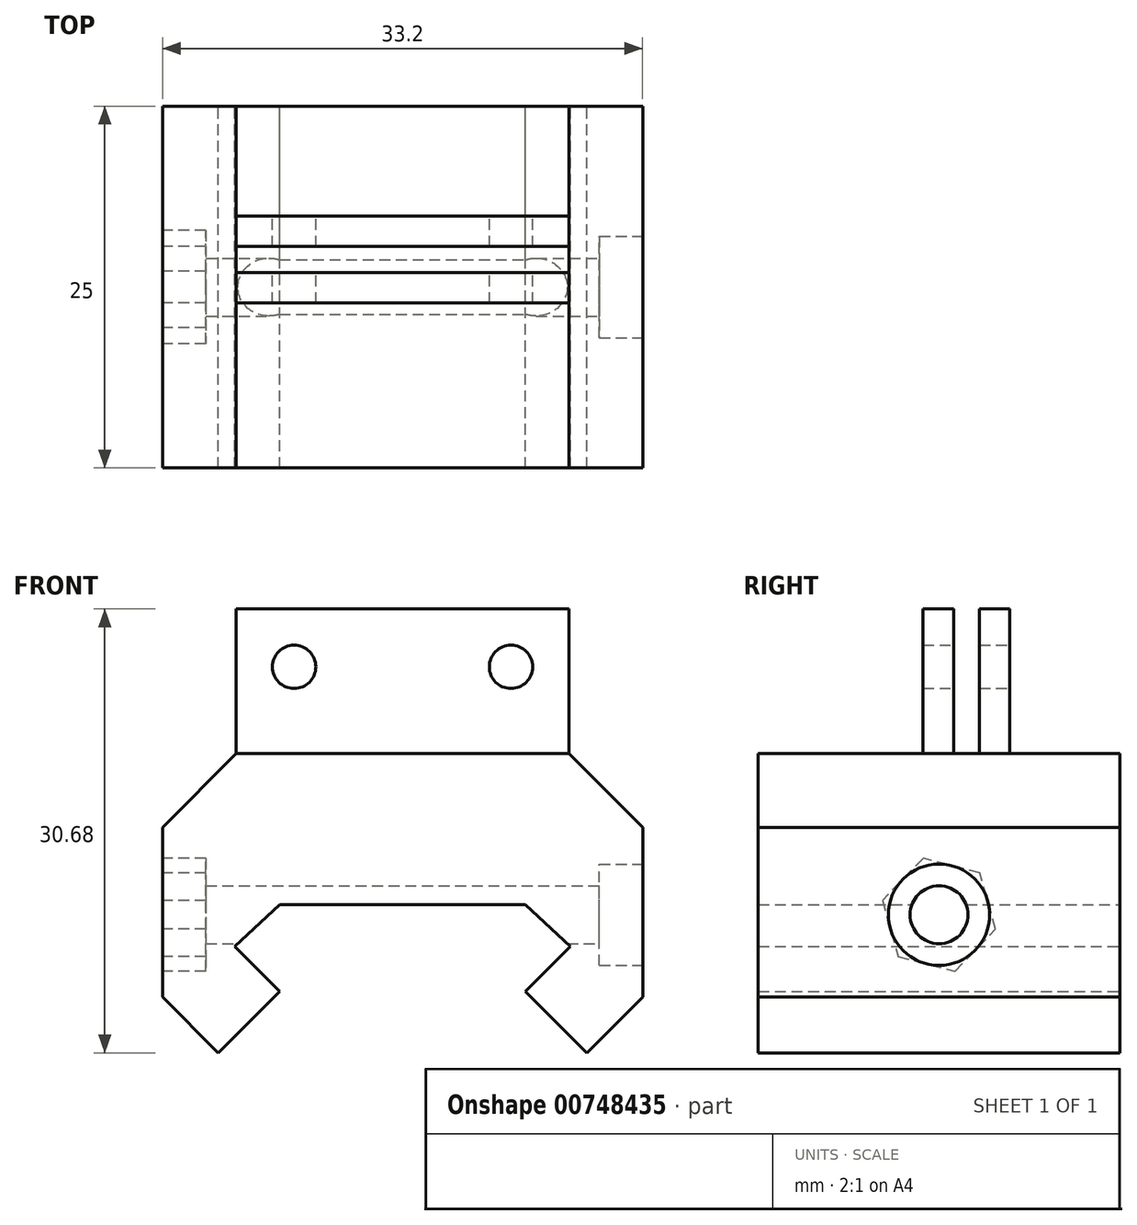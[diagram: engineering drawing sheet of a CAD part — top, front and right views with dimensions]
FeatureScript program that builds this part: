
annotation { "Feature Type Name" : "Feature", "Feature Type Description" : "" }
export const myFeature = defineFeature(function(context is Context, id is Id, definition is map)
    precondition{}
    {
        {
            var Q0;
            Q0=qCreatedBy(makeId("Front.planeOp"),FACE);
            var sketch = newSketch(context, id + "F0", { "sketchPlane" : qUnion([Q0])});
            skLineSegment(sketch, "E0", {"start": v(-8.5, 0) * mm, "end": v(8.5, 0) * mm});
            skLineSegment(sketch, "E1", {"start": v(-8.5, 0) * mm, "end": v(-11.6, -2.9) * mm});
            skLineSegment(sketch, "E2", {"start": v(-11.6, -2.9) * mm, "end": v(-8.5, -6) * mm});
            skLineSegment(sketch, "E3", {"start": v(-8.5, -6) * mm, "end": v(-12.74, -10.24) * mm});
            skLineSegment(sketch, "E4", {"start": v(-12.74, -10.24) * mm, "end": v(-22.46, -0.52) * mm});
            skLineSegment(sketch, "E5", {"start": v(-22.46, -0.52) * mm, "end": v(-11.5, 10.44) * mm});
            skLineSegment(sketch, "E6", {"start": v(-11.5, 10.44) * mm, "end": v(11.5, 10.44) * mm});
            skLineSegment(sketch, "E7", {"start": v(11.5, 10.44) * mm, "end": v(22.46, -0.52) * mm});
            skLineSegment(sketch, "E8", {"start": v(22.46, -0.52) * mm, "end": v(12.74, -10.24) * mm});
            skLineSegment(sketch, "E9", {"start": v(12.74, -10.24) * mm, "end": v(8.5, -6) * mm});
            skLineSegment(sketch, "E10", {"start": v(8.5, -6) * mm, "end": v(11.6, -2.9) * mm});
            skLineSegment(sketch, "E11", {"start": v(11.6, -2.9) * mm, "end": v(8.5, 0) * mm});
            skSolve(sketch);
        }
        {
            var Q0;
            Q0 = qSketchRegion(id + "F0", true);
            extrude(context, id + "F1", {"entities" : qUnion([Q0]), "depth" : 25 * mm, "offsetDistance" : 25 * mm});
        }
        {
            var Q0;
            Q0=makeQuery(id+"F1.opExtrude","CAP_FACE",FACE,{"disambiguationData":[OSD([sQuery(id+"F0.wireOp",EDGE,"E0"),sQuery(id+"F0.wireOp",EDGE,"E1"),sQuery(id+"F0.wireOp",EDGE,"E2"),sQuery(id+"F0.wireOp",EDGE,"E3"),sQuery(id+"F0.wireOp",EDGE,"E4"),sQuery(id+"F0.wireOp",EDGE,"E5"),sQuery(id+"F0.wireOp",EDGE,"E6"),sQuery(id+"F0.wireOp",EDGE,"E7"),sQuery(id+"F0.wireOp",EDGE,"E8"),sQuery(id+"F0.wireOp",EDGE,"E9"),sQuery(id+"F0.wireOp",EDGE,"E10"),sQuery(id+"F0.wireOp",EDGE,"E11")])],"isStart":false});
            var sketch = newSketch(context, id + "F2", { "sketchPlane" : qUnion([Q0])});
            skLineSegment(sketch, "E12.bottom", {"start": v(-24.2, 10) * mm, "end": v(-16.6, 10) * mm});
            skLineSegment(sketch, "E12.top", {"start": v(-24.2, -11.1) * mm, "end": v(-16.6, -11.1) * mm});
            skLineSegment(sketch, "E12.left", {"start": v(-24.2, 10) * mm, "end": v(-24.2, -11.1) * mm});
            skLineSegment(sketch, "E12.right", {"start": v(-16.6, 10) * mm, "end": v(-16.6, -11.1) * mm});
            skLineSegment(sketch, "E13.bottom", {"start": v(26.87, 13.5) * mm, "end": v(16.6, 13.5) * mm});
            skLineSegment(sketch, "E13.top", {"start": v(26.87, -16.6) * mm, "end": v(16.6, -16.6) * mm});
            skLineSegment(sketch, "E13.left", {"start": v(26.87, 13.5) * mm, "end": v(26.87, -16.6) * mm});
            skLineSegment(sketch, "E13.right", {"start": v(16.6, 13.5) * mm, "end": v(16.6, -16.6) * mm});
            skSolve(sketch);
        }
        {
            var Q0;
            Q0 = qSketchRegion(id + "F2", true);
            extrude(context, id + "F3", {"entities" : qUnion([Q0]), "operationType" : NewBodyOperationType.REMOVE, "oppositeDirection" : true, "depth" : 25 * mm, "offsetDistance" : 25 * mm});
        }
        {
            var Q0;
            Q0=makeQuery(id+"F3.boolean.opBoolean","COPY",FACE,{"derivedFrom":makeQuery(id+"F3.opExtrude","SWEPT_FACE",FACE,{"disambiguationData":[OSD([sQuery(id+"F2.wireOp",EDGE,"E13.right")])]})});
            var sketch = newSketch(context, id + "F4", { "sketchPlane" : qUnion([Q0])});
            skCircle(sketch, "E14", {"center": v(-12.5, -0.7) * mm, "radius": 2 * mm});
            skSolve(sketch);
        }
        {
            var Q0;
            Q0 = qSketchRegion(id + "F4", true);
            extrude(context, id + "F5", {"entities" : qUnion([Q0]), "operationType" : NewBodyOperationType.REMOVE, "oppositeDirection" : true, "depth" : 35 * mm, "offsetDistance" : 25 * mm});
        }
        {
            var Q0;
            Q0=makeQuery(id+"F3.boolean.opBoolean","COPY",FACE,{"derivedFrom":makeQuery(id+"F3.opExtrude","SWEPT_FACE",FACE,{"disambiguationData":[OSD([sQuery(id+"F2.wireOp",EDGE,"E13.right")])]})});
            var sketch = newSketch(context, id + "F6", { "sketchPlane" : qUnion([Q0])});
            skCircle(sketch, "E15", {"center": v(-12.5, -0.7) * mm, "radius": 3.5 * mm});
            skSolve(sketch);
        }
        {
            var Q0;
            Q0 = qSketchRegion(id + "F6", true);
            extrude(context, id + "F7", {"entities" : qUnion([Q0]), "operationType" : NewBodyOperationType.REMOVE, "oppositeDirection" : true, "depth" : 3 * mm, "offsetDistance" : 25 * mm});
        }
        {
            var Q0;
            Q0=makeQuery(id+"F3.boolean.opBoolean","COPY",FACE,{"derivedFrom":makeQuery(id+"F3.opExtrude","SWEPT_FACE",FACE,{"disambiguationData":[OSD([sQuery(id+"F2.wireOp",EDGE,"E12.right")])]})});
            var sketch = newSketch(context, id + "F8", { "sketchPlane" : qUnion([Q0])});
            skCircle(sketch, "E16.cCircle", {"center": v(12.5, -0.7) * mm, "radius": 3.5 * mm, "construction": true});
            skLineSegment(sketch, "E16.0", {"start": v(16.42, 0.3) * mm, "end": v(15.32, -3.59) * mm});
            skLineSegment(sketch, "E16.1", {"start": v(15.32, -3.59) * mm, "end": v(11.4, -4.59) * mm});
            skLineSegment(sketch, "E16.2", {"start": v(11.4, -4.59) * mm, "end": v(8.58, -1.7) * mm});
            skLineSegment(sketch, "E16.3", {"start": v(8.58, -1.7) * mm, "end": v(9.68, 2.2) * mm});
            skLineSegment(sketch, "E16.4", {"start": v(9.68, 2.2) * mm, "end": v(13.6, 3.2) * mm});
            skLineSegment(sketch, "E16.5", {"start": v(13.6, 3.2) * mm, "end": v(16.42, 0.3) * mm});
            skPoint(sketch, "E16.0.midPoint", {"position": v(15.87, -1.64) * mm});
            skSolve(sketch);
        }
        {
            var Q0;
            Q0 = qSketchRegion(id + "F8", true);
            extrude(context, id + "F9", {"entities" : qUnion([Q0]), "operationType" : NewBodyOperationType.REMOVE, "oppositeDirection" : true, "depth" : 3 * mm, "offsetDistance" : 25 * mm});
        }
        {
            var Q0;
            Q0=makeQuery(id+"F1.opExtrude","SWEPT_FACE",FACE,{"disambiguationData":[OSD([sQuery(id+"F0.wireOp",EDGE,"E6")])]});
            var sketch = newSketch(context, id + "F10", { "sketchPlane" : qUnion([Q0])});
            skLineSegment(sketch, "E17.bottom", {"start": v(-11.5, -7.6) * mm, "end": v(11.5, -7.6) * mm});
            skLineSegment(sketch, "E17.top", {"start": v(-11.5, -13.6) * mm, "end": v(11.5, -13.6) * mm});
            skLineSegment(sketch, "E17.left", {"start": v(-11.5, -7.6) * mm, "end": v(-11.5, -13.6) * mm});
            skLineSegment(sketch, "E17.right", {"start": v(11.5, -7.6) * mm, "end": v(11.5, -13.6) * mm});
            skSolve(sketch);
        }
        {
            var Q0;
            Q0 = qSketchRegion(id + "F10", true);
            extrude(context, id + "F11", {"entities" : qUnion([Q0]), "operationType" : NewBodyOperationType.ADD, "depth" : 10 * mm, "offsetDistance" : 25 * mm});
        }
        {
            var Q0;
            Q0=makeQuery(id+"F11.opExtrude","CAP_FACE",FACE,{"disambiguationData":[OSD([sQuery(id+"F10.wireOp",EDGE,"E17.bottom"),sQuery(id+"F10.wireOp",EDGE,"E17.top"),sQuery(id+"F10.wireOp",EDGE,"E17.left"),sQuery(id+"F10.wireOp",EDGE,"E17.right")])],"isStart":false});
            var sketch = newSketch(context, id + "F12", { "sketchPlane" : qUnion([Q0])});
            skLineSegment(sketch, "E18.bottom", {"start": v(-11.5, -9.7) * mm, "end": v(11.5, -9.7) * mm});
            skLineSegment(sketch, "E18.top", {"start": v(-11.5, -11.5) * mm, "end": v(11.5, -11.5) * mm});
            skLineSegment(sketch, "E18.left", {"start": v(-11.5, -9.7) * mm, "end": v(-11.5, -11.5) * mm});
            skLineSegment(sketch, "E18.right", {"start": v(11.5, -9.7) * mm, "end": v(11.5, -11.5) * mm});
            skSolve(sketch);
        }
        {
            var Q0;
            Q0 = qSketchRegion(id + "F12", true);
            extrude(context, id + "F13", {"entities" : qUnion([Q0]), "operationType" : NewBodyOperationType.REMOVE, "oppositeDirection" : true, "depth" : 10 * mm, "offsetDistance" : 25 * mm});
        }
        {
            var Q0;
            Q0=makeQuery(id+"F11.opExtrude","SWEPT_FACE",FACE,{"disambiguationData":[OSD([sQuery(id+"F10.wireOp",EDGE,"E17.bottom")])]});
            var sketch = newSketch(context, id + "F14", { "sketchPlane" : qUnion([Q0])});
            skCircle(sketch, "E19", {"center": v(-7.5, 16.44) * mm, "radius": 1.5 * mm});
            skCircle(sketch, "E20", {"center": v(7.5, 16.44) * mm, "radius": 1.5 * mm});
            skSolve(sketch);
        }
        {
            var Q0;
            Q0 = qSketchRegion(id + "F14", true);
            extrude(context, id + "F15", {"entities" : qUnion([Q0]), "operationType" : NewBodyOperationType.REMOVE, "oppositeDirection" : true, "depth" : 25 * mm, "offsetDistance" : 25 * mm});
        }
    });
